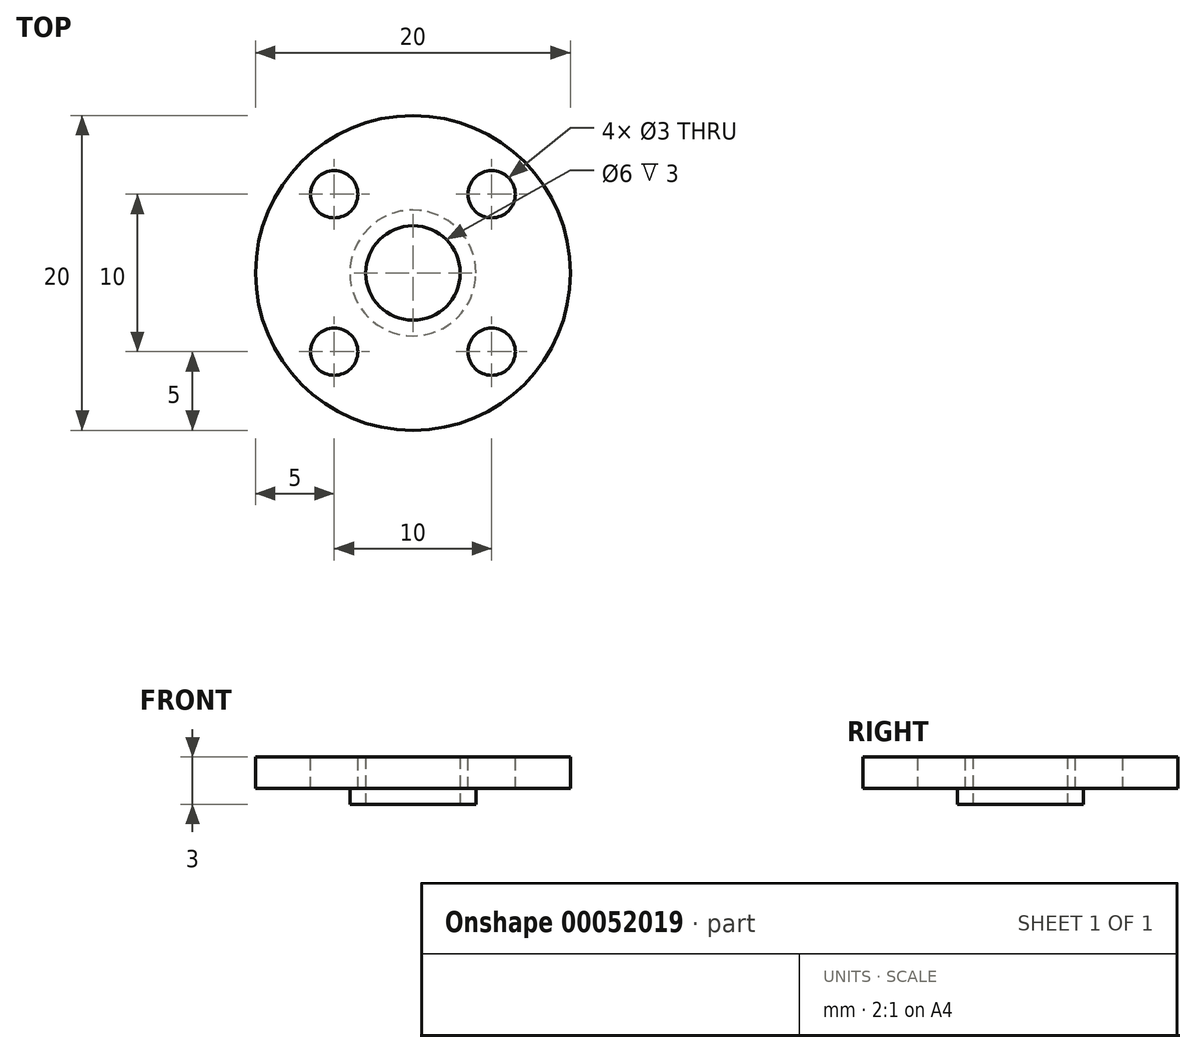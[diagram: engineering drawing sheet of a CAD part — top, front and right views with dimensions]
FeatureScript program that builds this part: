
annotation { "Feature Type Name" : "Feature", "Feature Type Description" : "" }
export const myFeature = defineFeature(function(context is Context, id is Id, definition is map)
    precondition{}
    {
        {
            var Q0;
            Q0=qCreatedBy(makeId("Top.planeOp"),FACE);
            var sketch = newSketch(context, id + "F0", { "sketchPlane" : qUnion([Q0])});
            skCircle(sketch, "E0", {"center": v(0, 0) * mm, "radius": 10 * mm});
            skCircle(sketch, "E1", {"center": v(0, 0) * mm, "radius": 3 * mm});
            skSolve(sketch);
        }
        {
            var Q0;
            Q0=makeQuery(id+"F0.imprint","IMPRINT",FACE,{"disambiguationData":[TD([[makeQuery(id+"F0.imprint","IMPRINT",EDGE,{"derivedFrom":sQuery(id+"F0.wireOp",EDGE,"E0")}),1.0]])]});
            extrude(context, id + "F1", {"entities" : qUnion([Q0]), "depth" : 2 * mm});
        }
        {
            var Q0;
            Q0=makeQuery(id+"F1.opExtrude","CAP_FACE",FACE,{"disambiguationData":[OSD([sQuery(id+"F0.wireOp",EDGE,"E0"),sQuery(id+"F0.wireOp",EDGE,"E1")])],"isStart":false});
            var sketch = newSketch(context, id + "F2", { "sketchPlane" : qUnion([Q0])});
            skLineSegment(sketch, "E2.bottom", {"start": v(-5, 5) * mm, "end": v(5, 5) * mm});
            skLineSegment(sketch, "E2.top", {"start": v(-5, -5) * mm, "end": v(5, -5) * mm});
            skLineSegment(sketch, "E2.left", {"start": v(-5, 5) * mm, "end": v(-5, -5) * mm});
            skLineSegment(sketch, "E2.right", {"start": v(5, 5) * mm, "end": v(5, -5) * mm});
            skLineSegment(sketch, "E3", {"start": v(-5, 5) * mm, "end": v(5, -5) * mm});
            skPoint(sketch, "E4", {"position": v(0, 0) * mm});
            skSolve(sketch);
        }
        {
            var Q0;
            Q0=sQuery(id+"F2.wireOp",VERTEX,"E2.left.start");
            var Q1;
            Q1=sQuery(id+"F2.wireOp",VERTEX,"E2.right.start");
            var Q2;
            Q2=sQuery(id+"F2.wireOp",VERTEX,"E2.top.end");
            var Q3;
            Q3=sQuery(id+"F2.wireOp",VERTEX,"E2.left.end");
            var Q4;
            Q4=makeQuery(id+"F1.opExtrude","SWEPT_BODY",BODY,{"disambiguationData":[OSD([sQuery(id+"F0.wireOp",EDGE,"E0"),sQuery(id+"F0.wireOp",EDGE,"E1")])]});
            hole(context, id + "F3", {"style" : HoleStyle.SIMPLE, "holeDiameter" : 3 * mm, "endStyle" : HoleEndStyle.THROUGH, "locations" : qUnion([Q0, Q1, Q2, Q3]), "scope" : qUnion([Q4]), "isTappedThrough" : true});
        }
        {
            var Q0;
            Q0=makeQuery(id+"F1.opExtrude","CAP_FACE",FACE,{"disambiguationData":[OSD([sQuery(id+"F0.wireOp",EDGE,"E0"),sQuery(id+"F0.wireOp",EDGE,"E1")])],"isStart":true});
            var sketch = newSketch(context, id + "F4", { "sketchPlane" : qUnion([Q0])});
            skCircle(sketch, "E5", {"center": v(0, 0) * mm, "radius": 4 * mm});
            skCircle(sketch, "E6", {"center": v(0, 0) * mm, "radius": 3 * mm});
            skSolve(sketch);
        }
        {
            var Q0;
            Q0=makeQuery(id+"F4.imprint","IMPRINT",FACE,{"disambiguationData":[TD([[makeQuery(id+"F4.imprint","IMPRINT",EDGE,{"derivedFrom":sQuery(id+"F4.wireOp",EDGE,"E5")}),1.0]])]});
            extrude(context, id + "F5", {"entities" : qUnion([Q0]), "operationType" : NewBodyOperationType.ADD, "depth" : 1 * mm});
        }
    });
